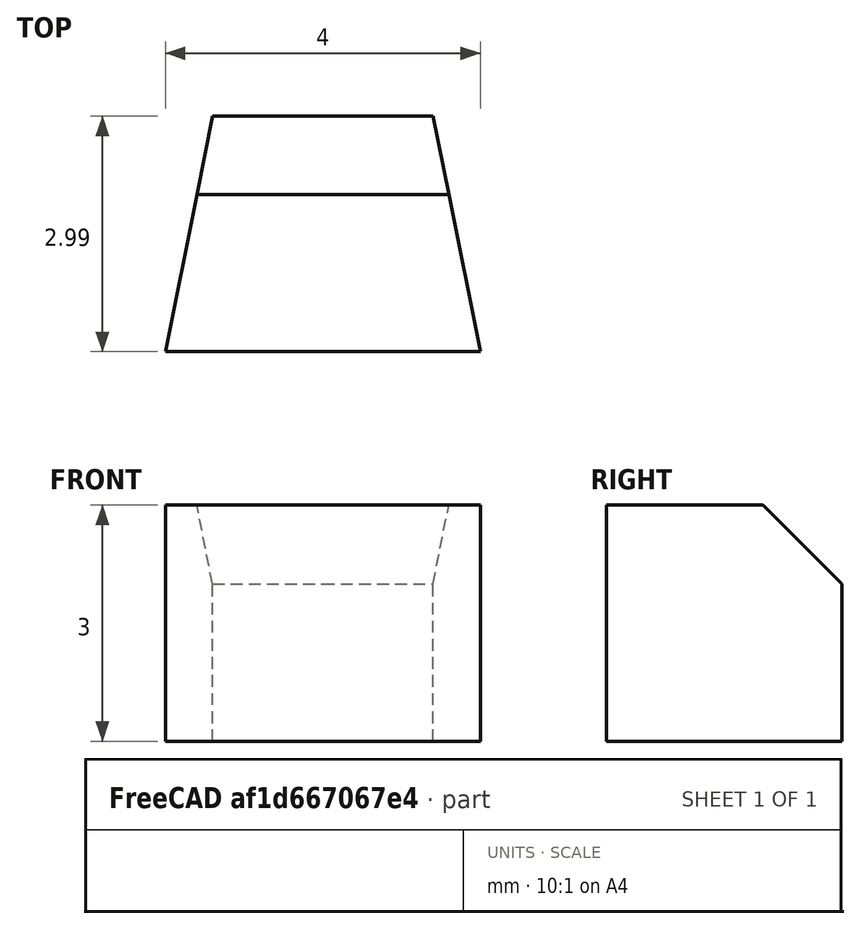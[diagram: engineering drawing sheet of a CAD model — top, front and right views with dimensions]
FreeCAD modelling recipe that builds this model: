
FCSTD DOCUMENT  (FreeCAD 0.18R4 (GitTag))
Label: room_clean
License: All rights reserved
LicenseURL: http://en.wikipedia.org/wiki/All_rights_reserved
objects: Sketcher::SketchObject×1, PartDesign::Pad×1, PartDesign::Chamfer×1, PartDesign::Body×1
note: 5 computed .brp shape members not serialized (recipe doc carries the construction recipe); baked Part::Feature solids carry a one-line shape summary decoded from their .brp

FEATURE [Sketcher::SketchObject] Sketch
  MapMode = 5
  Support = -> [XY_Plane]
  sketch-geometry (6):
    g0: LineSegment StartX=0 StartY=0 StartZ=0 EndX=2 EndY=0 EndZ=0
    g1: LineSegment StartX=2 StartY=0 StartZ=0 EndX=1.4 EndY=2.9922 EndZ=0
    g2: LineSegment StartX=1.4 StartY=2.9922 StartZ=0 EndX=0 EndY=2.9922 EndZ=0
    g3: LineSegment StartX=0 StartY=0 StartZ=0 EndX=-2 EndY=0 EndZ=0
    g4: LineSegment StartX=-2 StartY=0 StartZ=0 EndX=-1.4 EndY=2.9922 EndZ=0
    g5: LineSegment StartX=-1.4 StartY=2.9922 StartZ=0 EndX=0 EndY=2.9922 EndZ=0
  constraints (11):
    c: Coincident(g0,g-1)
    c: PointOnObject(g0,g-1)
    c: Coincident(g1,g0)
    c: Coincident(g2,g1)
    c: PointOnObject(g2,g-2)
    c: Horizontal(g2)
    c: DistanceX(g0,g0) = 2
    c: DistanceX(g2,g2) = 1.4
    c: Coincident(g4,g3)
    c: Coincident(g5,g4)
    c: Horizontal(g5)
FEATURE [PartDesign::Pad] Pad
  Length = 3
  Length2 = 100
  Profile = -> Sketch
  Type = 0
FEATURE [PartDesign::Chamfer] Chamfer
  Base = -> Pad [Edge13,Edge10]
  BaseFeature = -> Pad
  Size = 1
FEATURE [PartDesign::Body] Body
  Group = -> [Sketch,Pad,Chamfer]
  Origin = -> Origin
  Tip = -> Chamfer
